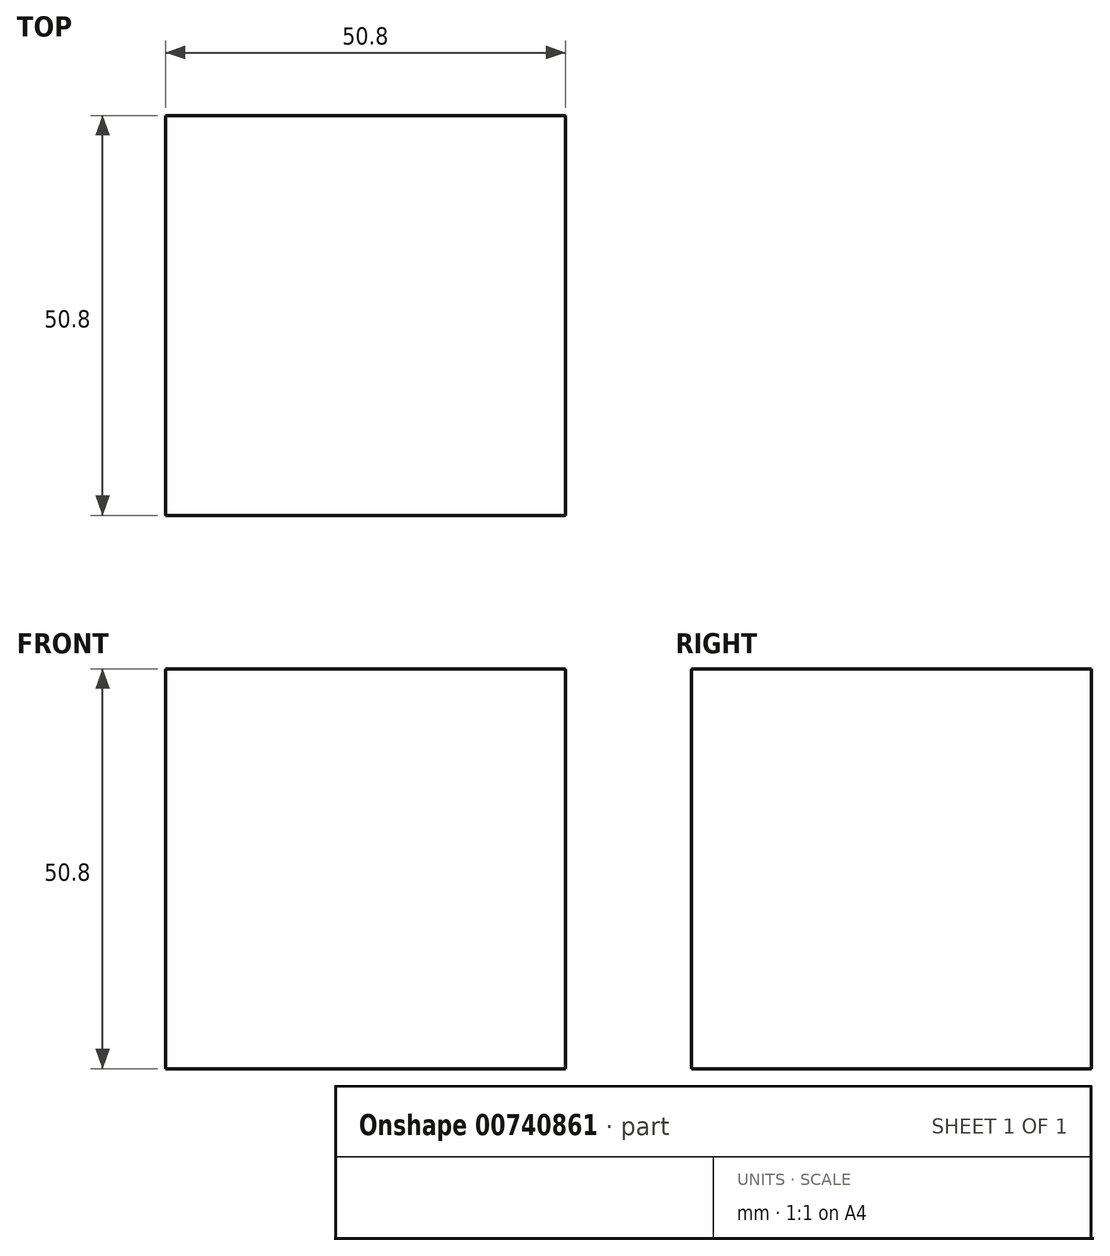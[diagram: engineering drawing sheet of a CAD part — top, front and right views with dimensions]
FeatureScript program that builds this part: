
annotation { "Feature Type Name" : "Feature", "Feature Type Description" : "" }
export const myFeature = defineFeature(function(context is Context, id is Id, definition is map)
    precondition{}
    {
        {
            var Q0;
            Q0=qCreatedBy(makeId("Top.planeOp"),FACE);
            var sketch = newSketch(context, id + "F0", { "sketchPlane" : qUnion([Q0])});
            skLineSegment(sketch, "E0.bottom", {"start": v(25.4, 25.4) * mm, "end": v(-25.4, 25.4) * mm});
            skLineSegment(sketch, "E0.top", {"start": v(25.4, -25.4) * mm, "end": v(-25.4, -25.4) * mm});
            skLineSegment(sketch, "E0.left", {"start": v(25.4, 25.4) * mm, "end": v(25.4, -25.4) * mm});
            skLineSegment(sketch, "E0.right", {"start": v(-25.4, 25.4) * mm, "end": v(-25.4, -25.4) * mm});
            skPoint(sketch, "E0.middle", {"position": v(0, 0) * mm});
            skSolve(sketch);
        }
        {
            var Q0;
            Q0=makeQuery(id+"F0.imprint","IMPRINT",FACE,{"disambiguationData":[TD([[makeQuery(id+"F0.imprint","IMPRINT",EDGE,{"derivedFrom":sQuery(id+"F0.wireOp",EDGE,"E0.bottom")}),1.0]])]});
            extrude(context, id + "F1", {"entities" : qUnion([Q0]), "depth" : 50.8 * mm, "offsetDistance" : 25.4 * mm});
        }
    });
